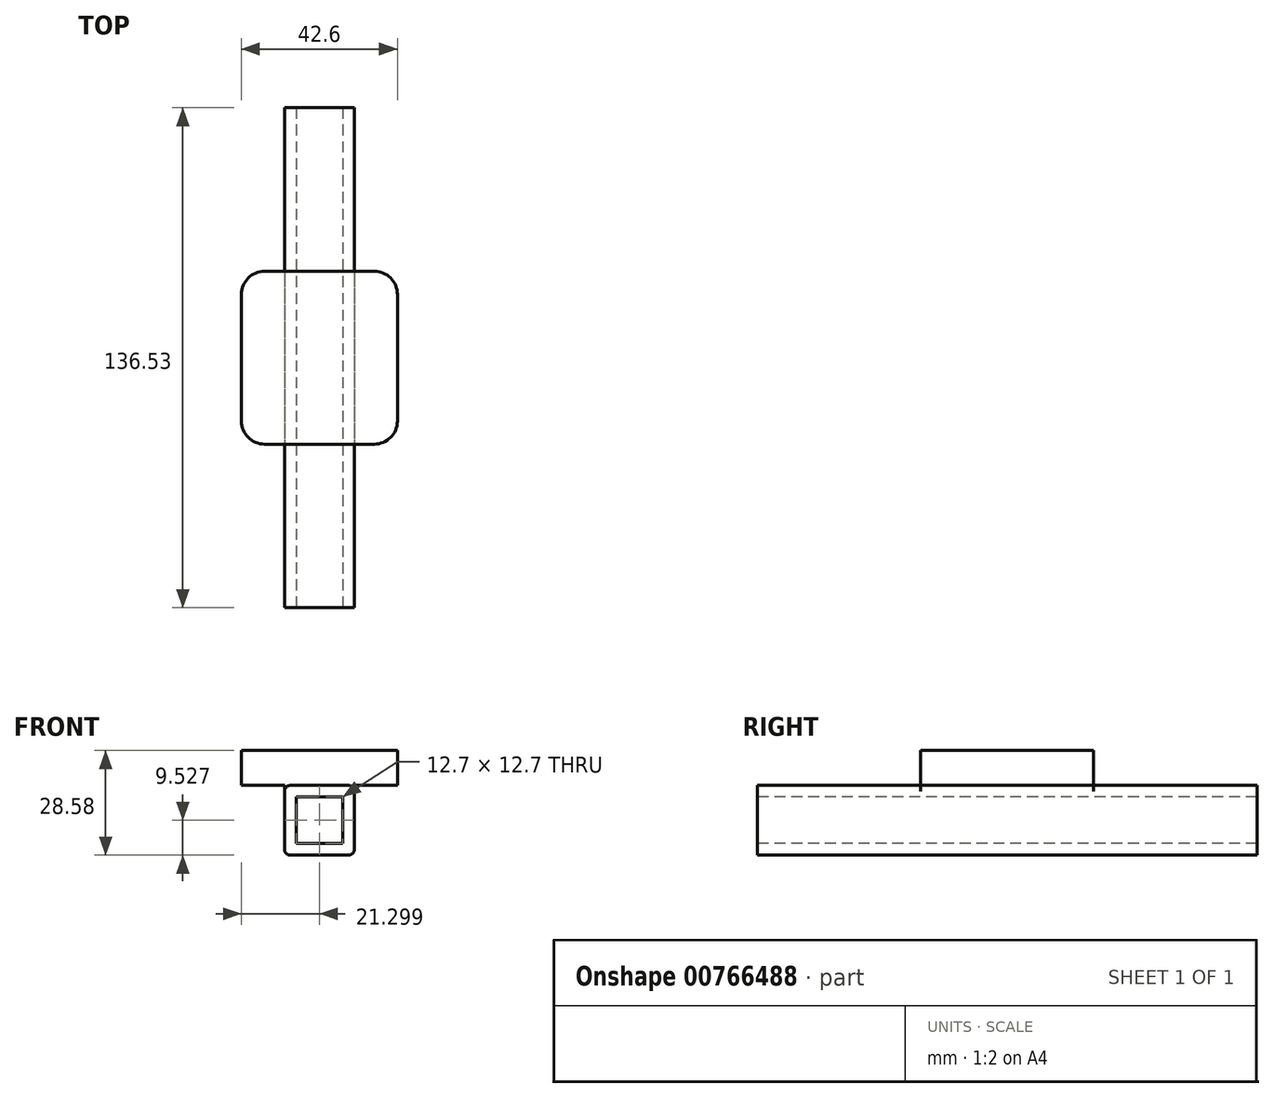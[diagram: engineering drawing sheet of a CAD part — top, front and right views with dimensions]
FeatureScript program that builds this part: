
annotation { "Feature Type Name" : "Feature", "Feature Type Description" : "" }
export const myFeature = defineFeature(function(context is Context, id is Id, definition is map)
    precondition{}
    {
        {
            var Q0;
            Q0=qCreatedBy(makeId("Front.planeOp"),FACE);
            var sketch = newSketch(context, id + "F0", { "sketchPlane" : qUnion([Q0])});
            skLineSegment(sketch, "E0.bottom", {"start": v(58.5, -61.68) * mm, "end": v(77.55, -61.68) * mm});
            skLineSegment(sketch, "E0.top", {"start": v(58.5, -42.63) * mm, "end": v(77.55, -42.63) * mm});
            skLineSegment(sketch, "E0.left", {"start": v(58.5, -61.68) * mm, "end": v(58.5, -42.63) * mm});
            skLineSegment(sketch, "E0.right", {"start": v(77.55, -61.68) * mm, "end": v(77.55, -42.63) * mm});
            skLineSegment(sketch, "E1.0", {"start": v(61.68, -45.8) * mm, "end": v(74.38, -45.8) * mm});
            skLineSegment(sketch, "E1.1", {"start": v(61.68, -58.5) * mm, "end": v(61.68, -45.8) * mm});
            skLineSegment(sketch, "E1.2", {"start": v(61.68, -58.5) * mm, "end": v(74.38, -58.5) * mm});
            skLineSegment(sketch, "E1.3", {"start": v(74.38, -58.5) * mm, "end": v(74.38, -45.8) * mm});
            skSolve(sketch);
        }
        {
            var Q0;
            Q0=qSketchRegion(id+"F0",true);
            extrude(context, id + "F1", {"entities" : qUnion([Q0]), "oppositeDirection" : true, "depth" : 136.53 * mm, "offsetDistance" : 25.4 * mm});
        }
        {
            var Q0;
            Q0=makeQuery(id+"F1.opExtrude","SWEPT_FACE",FACE,{"disambiguationData":[OSD([sQuery(id+"F0.wireOp",EDGE,"E0.top")])]});
            var sketch = newSketch(context, id + "F2", { "sketchPlane" : qUnion([Q0])});
            skLineSegment(sketch, "E2.bottom", {"start": v(46.73, 44.64) * mm, "end": v(89.33, 44.64) * mm});
            skLineSegment(sketch, "E2.top", {"start": v(46.73, 91.88) * mm, "end": v(89.33, 91.88) * mm});
            skLineSegment(sketch, "E2.left", {"start": v(46.73, 44.64) * mm, "end": v(46.73, 91.88) * mm});
            skLineSegment(sketch, "E2.right", {"start": v(89.33, 44.64) * mm, "end": v(89.33, 91.88) * mm});
            skSolve(sketch);
        }
        {
            var Q0;
            Q0=qSketchRegion(id+"F2",true);
            extrude(context, id + "F3", {"entities" : qUnion([Q0]), "operationType" : NewBodyOperationType.ADD, "depth" : 9.52 * mm, "offsetDistance" : 25.4 * mm});
        }
        {
            var Q0;
            Q0=makeQuery(id+"F3.opExtrude","SWEPT_EDGE",EDGE,{"disambiguationData":[OSD([sQuery(id+"F2.wireOp",EDGE,"E2.bottom"),sQuery(id+"F2.wireOp",EDGE,"E2.right")])]});
            var Q1;
            Q1=makeQuery(id+"F3.opExtrude","SWEPT_EDGE",EDGE,{"disambiguationData":[OSD([sQuery(id+"F2.wireOp",EDGE,"E2.top"),sQuery(id+"F2.wireOp",EDGE,"E2.right")])]});
            var Q2;
            Q2=makeQuery(id+"F3.opExtrude","SWEPT_EDGE",EDGE,{"disambiguationData":[OSD([sQuery(id+"F2.wireOp",EDGE,"E2.bottom"),sQuery(id+"F2.wireOp",EDGE,"E2.left")])]});
            var Q3;
            Q3=makeQuery(id+"F3.opExtrude","SWEPT_EDGE",EDGE,{"disambiguationData":[OSD([sQuery(id+"F2.wireOp",EDGE,"E2.top"),sQuery(id+"F2.wireOp",EDGE,"E2.left")])]});
            fillet(context, id + "F4", {"entities" : qUnion([Q0, Q1, Q2, Q3]), "radius" : 6.35 * mm, "tangentPropagation" : true, "allowEdgeOverflow" : false});
        }
        {
            var Q0;
            {var subQ0=sQuery(id+"F2.wireOp",EDGE,"E2.bottom");var subQ1=sQuery(id+"F0.wireOp",EDGE,"E0.right");var subQ2=makeQuery(id+"F1.opExtrude","SWEPT_FACE",FACE,{"disambiguationData":[OSD([subQ1])]});var subQ3=sQuery(id+"F0.wireOp",EDGE,"E0.top");var subQ4=makeQuery(id+"F1.opExtrude","SWEPT_FACE",FACE,{"disambiguationData":[OSD([subQ3])]});Q0=makeQuery(id+"F3.boolean.opBoolean","SPLIT",EDGE,{"disambiguationData":[topologyDisambiguationEdgeConnected([subQ4,subQ2]),TD([makeQuery(id+"F3.opExtrude","SWEPT_FACE",FACE,{"disambiguationData":[OSD([subQ0])]})])],"derivedFrom":makeQuery(id+"F1.opExtrude","SWEPT_EDGE",EDGE,{"disambiguationData":[OSD([subQ3,subQ1])]})});}
            var Q1;
            Q1=makeQuery(id+"F1.opExtrude","SWEPT_EDGE",EDGE,{"disambiguationData":[OSD([sQuery(id+"F0.wireOp",EDGE,"E0.bottom"),sQuery(id+"F0.wireOp",EDGE,"E0.right")])]});
            var Q2;
            {var subQ0=sQuery(id+"F2.wireOp",EDGE,"E2.top");var subQ1=sQuery(id+"F0.wireOp",EDGE,"E0.left");var subQ2=makeQuery(id+"F1.opExtrude","SWEPT_FACE",FACE,{"disambiguationData":[OSD([subQ1])]});var subQ3=sQuery(id+"F0.wireOp",EDGE,"E0.top");var subQ4=makeQuery(id+"F1.opExtrude","SWEPT_FACE",FACE,{"disambiguationData":[OSD([subQ3])]});Q2=makeQuery(id+"F3.boolean.opBoolean","SPLIT",EDGE,{"disambiguationData":[topologyDisambiguationEdgeConnected([subQ4,subQ2]),TD([makeQuery(id+"F3.opExtrude","SWEPT_FACE",FACE,{"disambiguationData":[OSD([subQ0])]})])],"derivedFrom":makeQuery(id+"F1.opExtrude","SWEPT_EDGE",EDGE,{"disambiguationData":[OSD([subQ3,subQ1])]})});}
            var Q3;
            {var subQ0=sQuery(id+"F2.wireOp",EDGE,"E2.bottom");var subQ1=sQuery(id+"F0.wireOp",EDGE,"E0.left");var subQ2=makeQuery(id+"F1.opExtrude","SWEPT_FACE",FACE,{"disambiguationData":[OSD([subQ1])]});var subQ3=sQuery(id+"F0.wireOp",EDGE,"E0.top");var subQ4=makeQuery(id+"F1.opExtrude","SWEPT_FACE",FACE,{"disambiguationData":[OSD([subQ3])]});Q3=makeQuery(id+"F3.boolean.opBoolean","SPLIT",EDGE,{"disambiguationData":[topologyDisambiguationEdgeConnected([subQ4,subQ2]),TD([makeQuery(id+"F3.opExtrude","SWEPT_FACE",FACE,{"disambiguationData":[OSD([subQ0])]})])],"derivedFrom":makeQuery(id+"F1.opExtrude","SWEPT_EDGE",EDGE,{"disambiguationData":[OSD([subQ3,subQ1])]})});}
            var Q4;
            Q4=makeQuery(id+"F1.opExtrude","SWEPT_EDGE",EDGE,{"disambiguationData":[OSD([sQuery(id+"F0.wireOp",EDGE,"E0.bottom"),sQuery(id+"F0.wireOp",EDGE,"E0.left")])]});
            var Q5;
            {var subQ0=sQuery(id+"F2.wireOp",EDGE,"E2.top");var subQ1=sQuery(id+"F0.wireOp",EDGE,"E0.right");var subQ2=makeQuery(id+"F1.opExtrude","SWEPT_FACE",FACE,{"disambiguationData":[OSD([subQ1])]});var subQ3=sQuery(id+"F0.wireOp",EDGE,"E0.top");var subQ4=makeQuery(id+"F1.opExtrude","SWEPT_FACE",FACE,{"disambiguationData":[OSD([subQ3])]});Q5=makeQuery(id+"F3.boolean.opBoolean","SPLIT",EDGE,{"disambiguationData":[topologyDisambiguationEdgeConnected([subQ4,subQ2]),TD([makeQuery(id+"F3.opExtrude","SWEPT_FACE",FACE,{"disambiguationData":[OSD([subQ0])]})])],"derivedFrom":makeQuery(id+"F1.opExtrude","SWEPT_EDGE",EDGE,{"disambiguationData":[OSD([subQ3,subQ1])]})});}
            fillet(context, id + "F5", {"entities" : qUnion([Q0, Q1, Q2, Q3, Q4, Q5]), "radius" : 1.59 * mm, "tangentPropagation" : true, "allowEdgeOverflow" : false});
        }
    });
